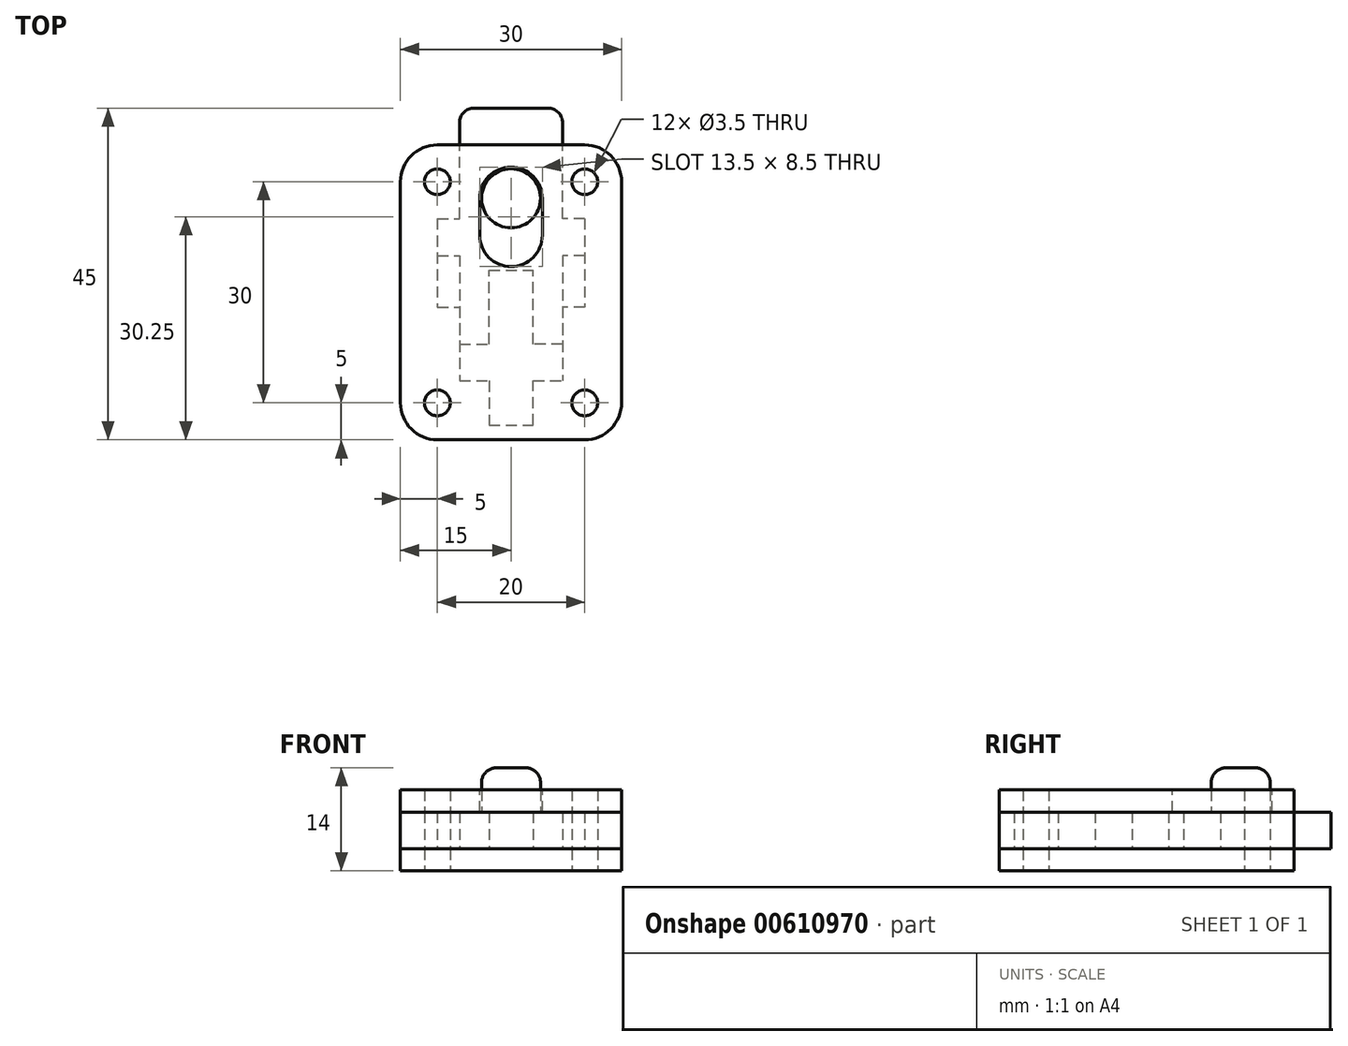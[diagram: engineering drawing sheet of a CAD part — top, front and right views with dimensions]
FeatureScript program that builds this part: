
annotation { "Feature Type Name" : "Feature", "Feature Type Description" : "" }
export const myFeature = defineFeature(function(context is Context, id is Id, definition is map)
    precondition{}
    {
        {
            var Q0;
            Q0=qCreatedBy(makeId("Top.planeOp"),FACE);
            var sketch = newSketch(context, id + "F0", { "sketchPlane" : qUnion([Q0])});
            skLineSegment(sketch, "E0.bottom", {"start": v(-10, 20) * mm, "end": v(10, 20) * mm});
            skLineSegment(sketch, "E0.top", {"start": v(-10, -20) * mm, "end": v(10, -20) * mm});
            skLineSegment(sketch, "E0.left", {"start": v(-15, 15) * mm, "end": v(-15, -15) * mm});
            skLineSegment(sketch, "E0.right", {"start": v(15, 15) * mm, "end": v(15, -15) * mm});
            skPoint(sketch, "E0.middle", {"position": v(0, 0) * mm});
            skPoint(sketch, "E1.visualSharp", {"position": v(-15, 20) * mm});
            skArc(sketch, "E1.filletArc", {"start": v(-10, 20) * mm, "mid": v(-13.54, 18.54) * mm, "end": v(-15, 15) * mm});
            skPoint(sketch, "E2.visualSharp", {"position": v(15, 20) * mm});
            skArc(sketch, "E2.filletArc", {"start": v(15, 15) * mm, "mid": v(13.54, 18.54) * mm, "end": v(10, 20) * mm});
            skPoint(sketch, "E3.visualSharp", {"position": v(15, -20) * mm});
            skArc(sketch, "E3.filletArc", {"start": v(10, -20) * mm, "mid": v(13.54, -18.54) * mm, "end": v(15, -15) * mm});
            skPoint(sketch, "E4.visualSharp", {"position": v(-15, -20) * mm});
            skArc(sketch, "E4.filletArc", {"start": v(-15, -15) * mm, "mid": v(-13.54, -18.54) * mm, "end": v(-10, -20) * mm});
            skCircle(sketch, "E5", {"center": v(-10, 15) * mm, "radius": 1.75 * mm});
            skCircle(sketch, "E6.MirrorC", {"center": v(10, 15) * mm, "radius": 1.75 * mm});
            skCircle(sketch, "E7.MirrorC", {"center": v(10, -15) * mm, "radius": 1.75 * mm});
            skCircle(sketch, "E8.MirrorC", {"center": v(-10, -15) * mm, "radius": 1.75 * mm});
            skSolve(sketch);
        }
        {
            var Q0;
            Q0 = qSketchRegion(id + "F0", true);
            extrude(context, id + "F1", {"entities" : qUnion([Q0]), "depth" : 3 * mm, "offsetDistance" : 25 * mm});
        }
        {
            var Q0;
            Q0=makeQuery(id+"F1.opExtrude","CAP_FACE",FACE,{"disambiguationData":[OSD([sQuery(id+"F0.wireOp",EDGE,"E0.bottom"),sQuery(id+"F0.wireOp",EDGE,"E0.top"),sQuery(id+"F0.wireOp",EDGE,"E0.left"),sQuery(id+"F0.wireOp",EDGE,"E0.right"),sQuery(id+"F0.wireOp",EDGE,"E1.filletArc"),sQuery(id+"F0.wireOp",EDGE,"E2.filletArc"),sQuery(id+"F0.wireOp",EDGE,"E3.filletArc"),sQuery(id+"F0.wireOp",EDGE,"E4.filletArc"),sQuery(id+"F0.wireOp",EDGE,"E5"),sQuery(id+"F0.wireOp",EDGE,"E6.MirrorC"),sQuery(id+"F0.wireOp",EDGE,"E7.MirrorC"),sQuery(id+"F0.wireOp",EDGE,"E8.MirrorC")])],"isStart":false});
            var sketch = newSketch(context, id + "F2", { "sketchPlane" : qUnion([Q0])});
            skLineSegment(sketch, "E9.bottom", {"start": v(-10, 20) * mm, "end": v(-7, 20) * mm});
            skLineSegment(sketch, "E9.top", {"start": v(-10, -20) * mm, "end": v(10, -20) * mm});
            skLineSegment(sketch, "E9.left", {"start": v(-15, 15) * mm, "end": v(-15, -15) * mm});
            skLineSegment(sketch, "E9.right", {"start": v(15, 15) * mm, "end": v(15, -15) * mm});
            skPoint(sketch, "E9.middle", {"position": v(0, 0) * mm});
            skArc(sketch, "E10.0.0", {"start": v(-15, -15) * mm, "mid": v(-13.54, -18.54) * mm, "end": v(-10, -20) * mm});
            skLineSegment(sketch, "E10.0.1", {"start": v(-10, -20) * mm, "end": v(-7, -20) * mm});
            skArc(sketch, "E10.0.2", {"start": v(10, -20) * mm, "mid": v(13.54, -18.54) * mm, "end": v(15, -15) * mm});
            skLineSegment(sketch, "E10.0.3", {"start": v(15, -15) * mm, "end": v(15, 15) * mm});
            skArc(sketch, "E10.0.4", {"start": v(15, 15) * mm, "mid": v(13.54, 18.54) * mm, "end": v(10, 20) * mm});
            skLineSegment(sketch, "E10.0.5", {"start": v(10, 20) * mm, "end": v(7, 20) * mm});
            skArc(sketch, "E10.0.6", {"start": v(-10, 20) * mm, "mid": v(-13.54, 18.54) * mm, "end": v(-15, 15) * mm});
            skPoint(sketch, "E11.visualSharp", {"position": v(-15, 20) * mm});
            skPoint(sketch, "E12.visualSharp", {"position": v(15, 20) * mm});
            skPoint(sketch, "E13.visualSharp", {"position": v(-15, -20) * mm});
            skPoint(sketch, "E14.visualSharp", {"position": v(15, -20) * mm});
            skCircle(sketch, "E15", {"center": v(-10, 15) * mm, "radius": 1.75 * mm});
            skCircle(sketch, "E16.MirrorC", {"center": v(10, 15) * mm, "radius": 1.75 * mm});
            skCircle(sketch, "E17.MirrorC", {"center": v(10, -15) * mm, "radius": 1.75 * mm});
            skCircle(sketch, "E18.MirrorC", {"center": v(-10, -15) * mm, "radius": 1.75 * mm});
            skLineSegment(sketch, "E19.top", {"start": v(-7, -20) * mm, "end": v(7, -20) * mm});
            skLineSegment(sketch, "E19.left", {"start": v(-7, 20) * mm, "end": v(-7, 10) * mm});
            skLineSegment(sketch, "E19.right", {"start": v(7, 20) * mm, "end": v(7, 10) * mm});
            skLineSegment(sketch, "E20", {"start": v(-7, -12) * mm, "end": v(-3, -12) * mm});
            skLineSegment(sketch, "E21.trimOffspring", {"start": v(7, -20) * mm, "end": v(10, -20) * mm});
            skPoint(sketch, "E22.orphan", {"position": v(-10, -12) * mm});
            skLineSegment(sketch, "E23.trimOffspring", {"start": v(7, 20) * mm, "end": v(10, 20) * mm});
            skLineSegment(sketch, "E24.trimOffspring", {"start": v(-7, 20) * mm, "end": v(-10, 20) * mm});
            skLineSegment(sketch, "E25", {"start": v(-10, 15) * mm, "end": v(-5.3, 15) * mm, "construction": true});
            skLineSegment(sketch, "E26.MirrorCS", {"start": v(-10, 25) * mm, "end": v(-5.3, 25) * mm});
            skLineSegment(sketch, "E27.MirrorCS", {"start": v(-10, 10) * mm, "end": v(-7, 10) * mm});
            skLineSegment(sketch, "E28.MirrorCS", {"start": v(-10, 25) * mm, "end": v(-5.3, 25) * mm, "construction": true});
            skLineSegment(sketch, "E29", {"start": v(-10, 10) * mm, "end": v(-10, -2) * mm});
            skLineSegment(sketch, "E30", {"start": v(-10, -2) * mm, "end": v(-7, -2) * mm});
            skLineSegment(sketch, "E31.trimOffspring", {"start": v(-7, -2) * mm, "end": v(-7, -12) * mm});
            skLineSegment(sketch, "E32.MirrorCS", {"start": v(10, -2) * mm, "end": v(7, -2) * mm});
            skLineSegment(sketch, "E33.MirrorCS", {"start": v(10, 10) * mm, "end": v(7, 10) * mm});
            skLineSegment(sketch, "E34.MirrorCS", {"start": v(10, 10) * mm, "end": v(10, -2) * mm});
            skLineSegment(sketch, "E35.trimOffspring", {"start": v(7, -2) * mm, "end": v(7, -12) * mm});
            skLineSegment(sketch, "E36", {"start": v(-3, -12) * mm, "end": v(-3, -18) * mm});
            skLineSegment(sketch, "E37", {"start": v(-3, -18) * mm, "end": v(3, -18) * mm});
            skLineSegment(sketch, "E38", {"start": v(3, -18) * mm, "end": v(3, -12) * mm});
            skLineSegment(sketch, "E39.trimOffspring", {"start": v(3, -12) * mm, "end": v(7, -12) * mm});
            skSolve(sketch);
        }
        {
            var Q0;
            Q0 = qSketchRegion(id + "F2", true);
            extrude(context, id + "F3", {"entities" : qUnion([Q0]), "depth" : 5 * mm, "offsetDistance" : 25 * mm});
        }
        {
            var Q0;
            Q0=makeQuery(id+"F1.opExtrude","CAP_FACE",FACE,{"disambiguationData":[OSD([sQuery(id+"F0.wireOp",EDGE,"E0.bottom"),sQuery(id+"F0.wireOp",EDGE,"E0.top"),sQuery(id+"F0.wireOp",EDGE,"E0.left"),sQuery(id+"F0.wireOp",EDGE,"E0.right"),sQuery(id+"F0.wireOp",EDGE,"E1.filletArc"),sQuery(id+"F0.wireOp",EDGE,"E2.filletArc"),sQuery(id+"F0.wireOp",EDGE,"E3.filletArc"),sQuery(id+"F0.wireOp",EDGE,"E4.filletArc"),sQuery(id+"F0.wireOp",EDGE,"E5"),sQuery(id+"F0.wireOp",EDGE,"E6.MirrorC"),sQuery(id+"F0.wireOp",EDGE,"E7.MirrorC"),sQuery(id+"F0.wireOp",EDGE,"E8.MirrorC")])],"isStart":false});
            var sketch = newSketch(context, id + "F4", { "sketchPlane" : qUnion([Q0])});
            skLineSegment(sketch, "E40.top", {"start": v(-3, 3) * mm, "end": v(3, 3) * mm});
            skLineSegment(sketch, "E40.left", {"start": v(-3, -7) * mm, "end": v(-3, 3) * mm});
            skLineSegment(sketch, "E41", {"start": v(-5, 25) * mm, "end": v(5, 25) * mm});
            skLineSegment(sketch, "E42", {"start": v(-10, 10) * mm, "end": v(-7, 10) * mm});
            skLineSegment(sketch, "E43", {"start": v(-10, 10) * mm, "end": v(-10, 5) * mm});
            skLineSegment(sketch, "E44", {"start": v(-10, 5) * mm, "end": v(-7, 5) * mm});
            skLineSegment(sketch, "E45.trimOffspring", {"start": v(-7, 10) * mm, "end": v(-7, 23) * mm});
            skLineSegment(sketch, "E46", {"start": v(-7, 5) * mm, "end": v(-7, -7) * mm});
            skPoint(sketch, "E47.MirrorCS.end.orphan", {"position": v(7, 25) * mm});
            skLineSegment(sketch, "E48.MirrorCS", {"start": v(10, 5) * mm, "end": v(7, 5) * mm});
            skLineSegment(sketch, "E49.MirrorCS", {"start": v(10, 10) * mm, "end": v(10, 5) * mm});
            skLineSegment(sketch, "E50.MirrorCS", {"start": v(7, 10) * mm, "end": v(7, 23) * mm});
            skLineSegment(sketch, "E51.MirrorCS", {"start": v(10, 10) * mm, "end": v(7, 10) * mm});
            skLineSegment(sketch, "E52", {"start": v(-7, -7) * mm, "end": v(-3, -7) * mm});
            skPoint(sketch, "E53.orphan", {"position": v(7, -12) * mm});
            skLineSegment(sketch, "E54.MirrorCS", {"start": v(7, 5) * mm, "end": v(7, -7) * mm});
            skLineSegment(sketch, "E55.MirrorCS", {"start": v(3, -7) * mm, "end": v(3, 3) * mm});
            skLineSegment(sketch, "E56.MirrorCS", {"start": v(7, -7) * mm, "end": v(3, -7) * mm});
            skPoint(sketch, "E57.visualSharp", {"position": v(-7, 25) * mm});
            skArc(sketch, "E57.filletArc", {"start": v(-5, 25) * mm, "mid": v(-6.41, 24.41) * mm, "end": v(-7, 23) * mm});
            skArc(sketch, "E58.filletArc", {"start": v(7, 23) * mm, "mid": v(6.41, 24.41) * mm, "end": v(5, 25) * mm});
            skSolve(sketch);
        }
        {
            var Q0;
            Q0=makeQuery(id+"F4.imprint","IMPRINT",FACE,{"disambiguationData":[TD([[makeQuery(id+"F4.imprint","IMPRINT",EDGE,{"derivedFrom":sQuery(id+"F4.wireOp",EDGE,"E41")}),-1.0]])]});
            var Q1;
            Q1=makeQuery(id+"F4.imprint","IMPRINT",FACE,{"disambiguationData":[TD([[makeQuery(id+"F4.imprint","IMPRINT",EDGE,{"derivedFrom":sQuery(id+"F4.wireOp",EDGE,"E40.top")}),1.0]])]});
            var Q2;
            Q2=sQuery(id+"F4.wireOp",EDGE,"Tmm5mXH2-HUf9-TBI8-dpue-bUEo293tKWZt");
            extrude(context, id + "F5", {"entities" : qUnion([Q0, Q1]), "surfaceEntities" : qUnion([Q2]), "depth" : 5 * mm, "offsetDistance" : 25 * mm});
        }
        {
            var Q0;
            Q0=makeQuery(id+"F5.opExtrude","CAP_FACE",FACE,{"disambiguationData":[OSD([sQuery(id+"F4.wireOp",EDGE,"E40.top"),sQuery(id+"F4.wireOp",EDGE,"E40.left"),sQuery(id+"F4.wireOp",EDGE,"E41"),sQuery(id+"F4.wireOp",EDGE,"E42"),sQuery(id+"F4.wireOp",EDGE,"E43"),sQuery(id+"F4.wireOp",EDGE,"E44"),sQuery(id+"F4.wireOp",EDGE,"E45.trimOffspring"),sQuery(id+"F4.wireOp",EDGE,"E46"),sQuery(id+"F4.wireOp",EDGE,"E48.MirrorCS"),sQuery(id+"F4.wireOp",EDGE,"E49.MirrorCS"),sQuery(id+"F4.wireOp",EDGE,"E50.MirrorCS"),sQuery(id+"F4.wireOp",EDGE,"E51.MirrorCS"),sQuery(id+"F4.wireOp",EDGE,"E52"),sQuery(id+"F4.wireOp",EDGE,"E54.MirrorCS"),sQuery(id+"F4.wireOp",EDGE,"E55.MirrorCS"),sQuery(id+"F4.wireOp",EDGE,"E56.MirrorCS"),sQuery(id+"F4.wireOp",EDGE,"E57.filletArc"),sQuery(id+"F4.wireOp",EDGE,"E58.filletArc")])],"isStart":false});
            var sketch = newSketch(context, id + "F6", { "sketchPlane" : qUnion([Q0])});
            skLineSegment(sketch, "E59.0.0", {"start": v(10, 20) * mm, "end": v(7, 20) * mm});
            skLineSegment(sketch, "E59.0.12", {"start": v(-7, 20) * mm, "end": v(-10, 20) * mm});
            skArc(sketch, "E59.0.13", {"start": v(-10, 20) * mm, "mid": v(-13.54, 18.54) * mm, "end": v(-15, 15) * mm});
            skLineSegment(sketch, "E59.0.14", {"start": v(-15, 15) * mm, "end": v(-15, -15) * mm});
            skArc(sketch, "E59.0.15", {"start": v(-15, -15) * mm, "mid": v(-13.54, -18.54) * mm, "end": v(-10, -20) * mm});
            skLineSegment(sketch, "E59.0.16", {"start": v(-10, -20) * mm, "end": v(10, -20) * mm});
            skArc(sketch, "E59.0.17", {"start": v(10, -20) * mm, "mid": v(13.54, -18.54) * mm, "end": v(15, -15) * mm});
            skLineSegment(sketch, "E59.0.18", {"start": v(15, -15) * mm, "end": v(15, 15) * mm});
            skArc(sketch, "E59.0.19", {"start": v(15, 15) * mm, "mid": v(13.54, 18.54) * mm, "end": v(10, 20) * mm});
            skPoint(sketch, "E59.0.10.end.orphan", {"position": v(-7, 10) * mm});
            skPoint(sketch, "E59.0.9.end.orphan", {"position": v(-10, 10) * mm});
            skPoint(sketch, "E59.0.8.end.orphan", {"position": v(-10, -2) * mm});
            skPoint(sketch, "E59.0.2.start.orphan", {"position": v(7, 10) * mm});
            skPoint(sketch, "E59.0.3.start.orphan", {"position": v(10, 10) * mm});
            skPoint(sketch, "E59.0.4.start.orphan", {"position": v(10, -2) * mm});
            skPoint(sketch, "E59.0.5.start.orphan", {"position": v(7, -2) * mm});
            skPoint(sketch, "E59.0.6.start.orphan", {"position": v(7, -12) * mm});
            skPoint(sketch, "E59.0.7.end.orphan", {"position": v(-7, -2) * mm});
            skPoint(sketch, "E59.0.7.start.orphan", {"position": v(-7, -12) * mm});
            skLineSegment(sketch, "E60", {"start": v(-7, 20) * mm, "end": v(7, 20) * mm});
            skCircle(sketch, "E61", {"center": v(-10, 15) * mm, "radius": 1.75 * mm});
            skCircle(sketch, "E62.MirrorC", {"center": v(10, 15) * mm, "radius": 1.75 * mm});
            skCircle(sketch, "E63.MirrorC", {"center": v(10, -15) * mm, "radius": 1.75 * mm});
            skCircle(sketch, "E64.MirrorC", {"center": v(-10, -15) * mm, "radius": 1.75 * mm});
            skSolve(sketch);
        }
        {
            var Q0;
            Q0 = qSketchRegion(id + "F6", true);
            extrude(context, id + "F7", {"entities" : qUnion([Q0]), "depth" : 3 * mm, "offsetDistance" : 25 * mm});
        }
        {
            var Q0;
            Q0=makeQuery(id+"F7.opExtrude","CAP_FACE",FACE,{"disambiguationData":[OSD([sQuery(id+"F6.wireOp",EDGE,"E59.0.0"),sQuery(id+"F6.wireOp",EDGE,"E59.0.12"),sQuery(id+"F6.wireOp",EDGE,"E59.0.13"),sQuery(id+"F6.wireOp",EDGE,"E59.0.14"),sQuery(id+"F6.wireOp",EDGE,"E59.0.15"),sQuery(id+"F6.wireOp",EDGE,"E59.0.16"),sQuery(id+"F6.wireOp",EDGE,"E59.0.17"),sQuery(id+"F6.wireOp",EDGE,"E59.0.18"),sQuery(id+"F6.wireOp",EDGE,"E59.0.19"),sQuery(id+"F6.wireOp",EDGE,"E60")])],"isStart":false});
            var sketch = newSketch(context, id + "F8", { "sketchPlane" : qUnion([Q0])});
            skArc(sketch, "E65", {"start": v(4.25, 12.75) * mm, "mid": v(0, 17) * mm, "end": v(-4.25, 12.75) * mm});
            skArc(sketch, "E66", {"start": v(-4.25, 7.75) * mm, "mid": v(0, 3.5) * mm, "end": v(4.25, 7.75) * mm});
            skLineSegment(sketch, "E67", {"start": v(-4.25, 12.75) * mm, "end": v(-4.25, 7.75) * mm});
            skLineSegment(sketch, "E68", {"start": v(4.25, 12.75) * mm, "end": v(4.25, 7.75) * mm});
            skSolve(sketch);
        }
        {
            var Q0;
            Q0 = qSketchRegion(id + "F8", true);
            extrude(context, id + "F9", {"entities" : qUnion([Q0]), "operationType" : NewBodyOperationType.REMOVE, "oppositeDirection" : true, "depth" : 3 * mm, "offsetDistance" : 25 * mm});
        }
        {
            var Q0;
            Q0=makeQuery(id+"F5.opExtrude","CAP_FACE",FACE,{"disambiguationData":[OSD([sQuery(id+"F4.wireOp",EDGE,"E40.top"),sQuery(id+"F4.wireOp",EDGE,"E40.left"),sQuery(id+"F4.wireOp",EDGE,"E41"),sQuery(id+"F4.wireOp",EDGE,"E42"),sQuery(id+"F4.wireOp",EDGE,"E43"),sQuery(id+"F4.wireOp",EDGE,"E44"),sQuery(id+"F4.wireOp",EDGE,"E45.trimOffspring"),sQuery(id+"F4.wireOp",EDGE,"E46"),sQuery(id+"F4.wireOp",EDGE,"E48.MirrorCS"),sQuery(id+"F4.wireOp",EDGE,"E49.MirrorCS"),sQuery(id+"F4.wireOp",EDGE,"E50.MirrorCS"),sQuery(id+"F4.wireOp",EDGE,"E51.MirrorCS"),sQuery(id+"F4.wireOp",EDGE,"E52"),sQuery(id+"F4.wireOp",EDGE,"E54.MirrorCS"),sQuery(id+"F4.wireOp",EDGE,"E55.MirrorCS"),sQuery(id+"F4.wireOp",EDGE,"E56.MirrorCS"),sQuery(id+"F4.wireOp",EDGE,"E57.filletArc"),sQuery(id+"F4.wireOp",EDGE,"E58.filletArc")])],"isStart":false});
            var sketch = newSketch(context, id + "F10", { "sketchPlane" : qUnion([Q0])});
            skCircle(sketch, "E69", {"center": v(0, 12.75) * mm, "radius": 4 * mm});
            skPoint(sketch, "E70.0.end.orphan", {"position": v(-4.25, 12.75) * mm});
            skPoint(sketch, "E70.0.start.orphan", {"position": v(4.25, 12.75) * mm});
            skSolve(sketch);
        }
        {
            var Q0;
            Q0 = qSketchRegion(id + "F10", true);
            extrude(context, id + "F11", {"entities" : qUnion([Q0]), "operationType" : NewBodyOperationType.ADD, "depth" : 6 * mm, "offsetDistance" : 25 * mm});
        }
        {
            var Q0;
            Q0=makeQuery(id+"F11.opExtrude","CAP_EDGE",EDGE,{"disambiguationData":[OSD([sQuery(id+"F10.wireOp",EDGE,"E69")])],"isStart":false});
            fillet(context, id + "F12", {"entities" : qUnion([Q0]), "radius" : 2 * mm, "tangentPropagation" : true, "allowEdgeOverflow" : false});
        }
    });
